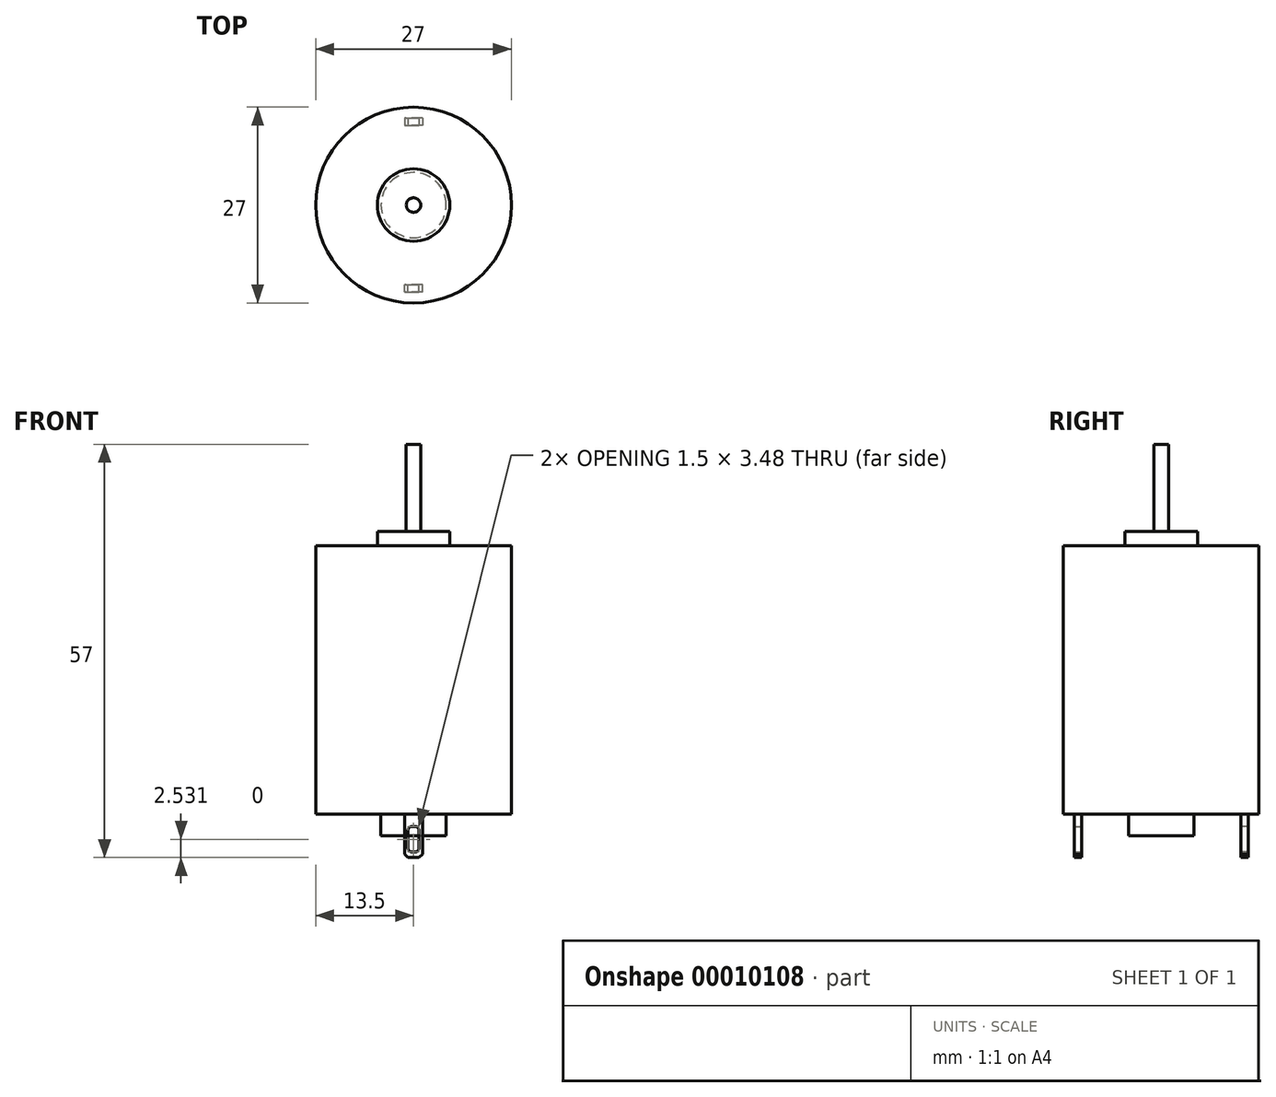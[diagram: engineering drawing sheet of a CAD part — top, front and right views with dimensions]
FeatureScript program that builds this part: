
annotation { "Feature Type Name" : "Feature", "Feature Type Description" : "" }
export const myFeature = defineFeature(function(context is Context, id is Id, definition is map)
    precondition{}
    {
        {
            var Q0;
            Q0=qCreatedBy(makeId("Top.planeOp"),FACE);
            var sketch = newSketch(context, id + "F0", { "sketchPlane" : qUnion([Q0])});
            skCircle(sketch, "E0", {"center": v(0, 0) * mm, "radius": 13.5 * mm});
            skSolve(sketch);
        }
        {
            var Q0;
            Q0=makeQuery(id+"F0.imprint","IMPRINT",FACE,{"disambiguationData":[TD([[makeQuery(id+"F0.imprint","IMPRINT",EDGE,{"derivedFrom":sQuery(id+"F0.wireOp",EDGE,"E0")}),1.0]])]});
            extrude(context, id + "F1", {"entities" : qUnion([Q0]), "depth" : 37 * mm});
        }
        {
            var Q0;
            Q0=makeQuery(id+"F1.opExtrude","CAP_FACE",FACE,{"disambiguationData":[OSD([sQuery(id+"F0.wireOp",EDGE,"E0")])],"isStart":false});
            var sketch = newSketch(context, id + "F2", { "sketchPlane" : qUnion([Q0])});
            skCircle(sketch, "E1", {"center": v(0, 0) * mm, "radius": 5 * mm});
            skSolve(sketch);
        }
        {
            var Q0;
            Q0=makeQuery(id+"F2.imprint","IMPRINT",FACE,{"disambiguationData":[TD([[makeQuery(id+"F2.imprint","IMPRINT",EDGE,{"derivedFrom":sQuery(id+"F2.wireOp",EDGE,"E1")}),1.0]])]});
            extrude(context, id + "F3", {"entities" : qUnion([Q0]), "operationType" : NewBodyOperationType.ADD, "depth" : 2 * mm});
        }
        {
            var Q0;
            Q0=makeQuery(id+"F3.opExtrude","CAP_FACE",FACE,{"disambiguationData":[OSD([sQuery(id+"F2.wireOp",EDGE,"E1")])],"isStart":false});
            var sketch = newSketch(context, id + "F4", { "sketchPlane" : qUnion([Q0])});
            skCircle(sketch, "E2", {"center": v(0, 0) * mm, "radius": 1 * mm});
            skSolve(sketch);
        }
        {
            var Q0;
            Q0=makeQuery(id+"F4.imprint","IMPRINT",FACE,{"disambiguationData":[TD([[makeQuery(id+"F4.imprint","IMPRINT",EDGE,{"derivedFrom":sQuery(id+"F4.wireOp",EDGE,"E2")}),1.0]])]});
            extrude(context, id + "F5", {"entities" : qUnion([Q0]), "operationType" : NewBodyOperationType.ADD, "depth" : 12 * mm});
        }
        {
            var Q0;
            Q0=makeQuery(id+"F1.opExtrude","CAP_FACE",FACE,{"disambiguationData":[OSD([sQuery(id+"F0.wireOp",EDGE,"E0")])],"isStart":true});
            var sketch = newSketch(context, id + "F6", { "sketchPlane" : qUnion([Q0])});
            skCircle(sketch, "E3", {"center": v(0, 0) * mm, "radius": 4.5 * mm});
            skSolve(sketch);
        }
        {
            var Q0;
            Q0=makeQuery(id+"F6.imprint","IMPRINT",FACE,{"disambiguationData":[TD([[makeQuery(id+"F6.imprint","IMPRINT",EDGE,{"derivedFrom":sQuery(id+"F6.wireOp",EDGE,"E3")}),1.0]])]});
            extrude(context, id + "F7", {"entities" : qUnion([Q0]), "operationType" : NewBodyOperationType.ADD, "depth" : 3 * mm});
        }
        {
            var Q0;
            Q0=qCreatedBy(makeId("Front.planeOp"),FACE);
            var sketch = newSketch(context, id + "F8", { "sketchPlane" : qUnion([Q0])});
            skLineSegment(sketch, "E4", {"start": v(-1.25, 0) * mm, "end": v(-1.25, -5.5) * mm});
            skLineSegment(sketch, "E5", {"start": v(-1.25, -5.5) * mm, "end": v(-0.75, -6) * mm});
            skLineSegment(sketch, "E6", {"start": v(0, 0) * mm, "end": v(-1.25, 0) * mm});
            skLineSegment(sketch, "E7", {"start": v(-0.75, -4.7) * mm, "end": v(-0.75, -2.23) * mm});
            skLineSegment(sketch, "E8", {"start": v(-0.25, -1.73) * mm, "end": v(0, -1.73) * mm});
            skLineSegment(sketch, "E9", {"start": v(0, -5.2) * mm, "end": v(-0.25, -5.2) * mm});
            skLineSegment(sketch, "E10", {"start": v(0, -6) * mm, "end": v(0, 0) * mm, "construction": true});
            skLineSegment(sketch, "E11", {"start": v(-0.75, -6) * mm, "end": v(0, -6) * mm});
            skLineSegment(sketch, "E12", {"start": v(-1.25, -6) * mm, "end": v(-0.75, -6) * mm, "construction": true});
            skPoint(sketch, "E13.visualSharp", {"position": v(-0.75, -5.2) * mm});
            skArc(sketch, "E13.filletArc", {"start": v(-0.75, -4.7) * mm, "mid": v(-0.6, -5.06) * mm, "end": v(-0.25, -5.2) * mm});
            skPoint(sketch, "E14.visualSharp", {"position": v(-0.75, -1.73) * mm});
            skArc(sketch, "E14.filletArc", {"start": v(-0.25, -1.73) * mm, "mid": v(-0.6, -1.88) * mm, "end": v(-0.75, -2.23) * mm});
            skLineSegment(sketch, "E15.0.MirrorCS", {"start": v(0.75, -6) * mm, "end": v(0, -6) * mm});
            skLineSegment(sketch, "E16.0.MirrorCS", {"start": v(1.25, -5.5) * mm, "end": v(0.75, -6) * mm});
            skLineSegment(sketch, "E17.0.MirrorCS", {"start": v(1.25, 0) * mm, "end": v(1.25, -5.5) * mm});
            skLineSegment(sketch, "E18.0.MirrorCS", {"start": v(0.25, -1.73) * mm, "end": v(0, -1.73) * mm});
            skArc(sketch, "E19.0.MirrorCS", {"start": v(0.25, -1.73) * mm, "mid": v(0.6, -1.88) * mm, "end": v(0.75, -2.23) * mm});
            skLineSegment(sketch, "E20.0.MirrorCS", {"start": v(0.75, -4.7) * mm, "end": v(0.75, -2.23) * mm});
            skArc(sketch, "E21.0.MirrorCS", {"start": v(0.75, -4.7) * mm, "mid": v(0.6, -5.06) * mm, "end": v(0.25, -5.2) * mm});
            skLineSegment(sketch, "E22.0.MirrorCS", {"start": v(0, -5.2) * mm, "end": v(0.25, -5.2) * mm});
            skLineSegment(sketch, "E23.0.MirrorCS", {"start": v(0, 0) * mm, "end": v(1.25, 0) * mm});
            skSolve(sketch);
        }
        {
            var Q0;
            Q0=makeQuery(id+"F8.imprint","IMPRINT",FACE,{"disambiguationData":[TD([[makeQuery(id+"F8.imprint","IMPRINT",EDGE,{"derivedFrom":sQuery(id+"F8.wireOp",EDGE,"E4")}),1.0]])]});
            extrude(context, id + "F9", {"entities" : qUnion([Q0]), "operationType" : NewBodyOperationType.ADD, "oppositeDirection" : true, "depth" : 12 * mm, "hasSecondDirection" : true, "secondDirectionOppositeDirection" : true, "secondDirectionDepth" : 11 * mm});
        }
        {
            var Q0;
            Q0=makeQuery(id+"F1.opExtrude","SWEPT_BODY",BODY,{"disambiguationData":[OSD([sQuery(id+"F0.wireOp",EDGE,"E0")])]});
            var Q1;
            Q1=qCreatedBy(makeId("Front.planeOp"),FACE);
            mirror(context, id + "F10", {"operationType" : NewBodyOperationType.ADD, "entities" : qUnion([Q0]), "mirrorPlane" : qUnion([Q1])});
        }
    });
